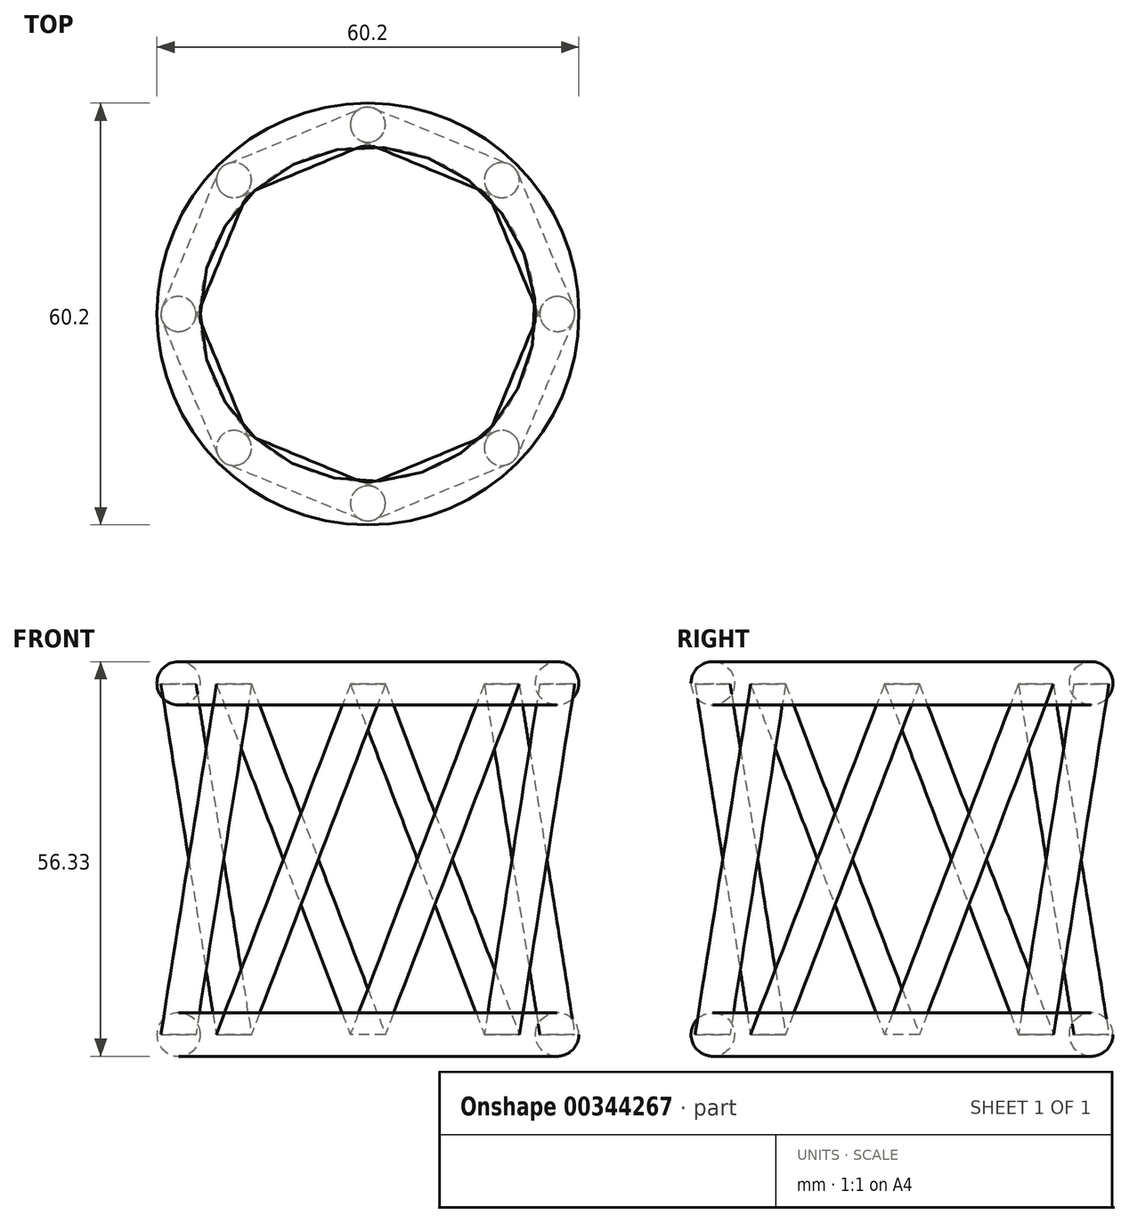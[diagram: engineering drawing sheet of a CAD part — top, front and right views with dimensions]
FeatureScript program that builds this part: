
annotation { "Feature Type Name" : "Feature", "Feature Type Description" : "" }
export const myFeature = defineFeature(function(context is Context, id is Id, definition is map)
    precondition{}
    {
        {
            var Q0;
            Q0=qCreatedBy(makeId("Top.planeOp"),FACE);
            var sketch = newSketch(context, id + "F0", { "sketchPlane" : qUnion([Q0])});
            skCircle(sketch, "E0", {"center": v(0, -27.04) * mm, "radius": 2.5 * mm});
            skCircle(sketch, "E1.1.0", {"center": v(10.35, -24.98) * mm, "radius": 2.5 * mm});
            skCircle(sketch, "E1.2.0", {"center": v(19.12, -19.12) * mm, "radius": 2.5 * mm});
            skCircle(sketch, "E1.3.0", {"center": v(24.98, -10.35) * mm, "radius": 2.5 * mm});
            skCircle(sketch, "E1.4.0", {"center": v(27.04, 0) * mm, "radius": 2.5 * mm});
            skCircle(sketch, "E1.5.0", {"center": v(24.98, 10.35) * mm, "radius": 2.5 * mm});
            skCircle(sketch, "E1.6.0", {"center": v(19.12, 19.12) * mm, "radius": 2.5 * mm});
            skCircle(sketch, "E1.7.0", {"center": v(10.35, 24.98) * mm, "radius": 2.5 * mm});
            skCircle(sketch, "E1.8.0", {"center": v(0, 27.04) * mm, "radius": 2.5 * mm});
            skCircle(sketch, "E1.9.0", {"center": v(-10.35, 24.98) * mm, "radius": 2.5 * mm});
            skCircle(sketch, "E1.10.0", {"center": v(-19.12, 19.12) * mm, "radius": 2.5 * mm});
            skCircle(sketch, "E1.11.0", {"center": v(-24.98, 10.35) * mm, "radius": 2.5 * mm});
            skCircle(sketch, "E1.12.0", {"center": v(-27.04, 0) * mm, "radius": 2.5 * mm});
            skCircle(sketch, "E1.13.0", {"center": v(-24.98, -10.35) * mm, "radius": 2.5 * mm});
            skCircle(sketch, "E1.14.0", {"center": v(-19.12, -19.12) * mm, "radius": 2.5 * mm});
            skCircle(sketch, "E1.15.0", {"center": v(-10.35, -24.98) * mm, "radius": 2.5 * mm});
            skPoint(sketch, "E1.center", {"position": v(0, 0) * mm});
            skLineSegment(sketch, "E2", {"start": v(0, -27.04) * mm, "end": v(0, 27.04) * mm});
            skSolve(sketch);
        }
        {
            var Q0;
            Q0=qCreatedBy(makeId("Top.planeOp"),FACE);
            cPlane(context, id + "F1", {"entities" : qUnion([Q0]), "cplaneType" : CPlaneType.OFFSET, "offset" : 50 * mm, "width" : 150 * mm, "height" : 150 * mm});
        }
        {
            var Q0;
            Q0=qCreatedBy(id+"F1.planeOp",FACE);
            var sketch = newSketch(context, id + "F2", { "sketchPlane" : qUnion([Q0])});
            skCircle(sketch, "E3", {"center": v(0, -27.02) * mm, "radius": 2.5 * mm});
            skCircle(sketch, "E4.1.0", {"center": v(10.34, -24.96) * mm, "radius": 2.5 * mm});
            skCircle(sketch, "E4.2.0", {"center": v(19.1, -19.1) * mm, "radius": 2.5 * mm});
            skCircle(sketch, "E4.3.0", {"center": v(24.96, -10.34) * mm, "radius": 2.5 * mm});
            skCircle(sketch, "E4.4.0", {"center": v(27.02, 0) * mm, "radius": 2.5 * mm});
            skCircle(sketch, "E4.5.0", {"center": v(24.96, 10.34) * mm, "radius": 2.5 * mm});
            skCircle(sketch, "E4.6.0", {"center": v(19.1, 19.1) * mm, "radius": 2.5 * mm});
            skCircle(sketch, "E4.7.0", {"center": v(10.34, 24.96) * mm, "radius": 2.5 * mm});
            skCircle(sketch, "E4.8.0", {"center": v(0, 27.02) * mm, "radius": 2.5 * mm});
            skCircle(sketch, "E4.9.0", {"center": v(-10.34, 24.96) * mm, "radius": 2.5 * mm});
            skCircle(sketch, "E4.10.0", {"center": v(-19.1, 19.1) * mm, "radius": 2.5 * mm});
            skCircle(sketch, "E4.11.0", {"center": v(-24.96, 10.34) * mm, "radius": 2.5 * mm});
            skCircle(sketch, "E4.12.0", {"center": v(-27.02, 0) * mm, "radius": 2.5 * mm});
            skCircle(sketch, "E4.13.0", {"center": v(-24.96, -10.34) * mm, "radius": 2.5 * mm});
            skCircle(sketch, "E4.14.0", {"center": v(-19.1, -19.1) * mm, "radius": 2.5 * mm});
            skCircle(sketch, "E4.15.0", {"center": v(-10.34, -24.96) * mm, "radius": 2.5 * mm});
            skPoint(sketch, "E4.center", {"position": v(0, 0) * mm});
            skLineSegment(sketch, "E5", {"start": v(19.1, -19.1) * mm, "end": v(-19.1, 19.1) * mm});
            skSolve(sketch);
        }
        {
            var Q0;
            Q0=sQuery(id+"F0.wireOp",VERTEX,"E0.center");
            var Q1;
            Q1=sQuery(id+"F2.wireOp",VERTEX,"E4.2.0.center");
            var Q2;
            Q2=sQuery(id+"F2.wireOp",VERTEX,"E5.end");
            cPlane(context, id + "F3", {"entities" : qUnion([Q0, Q1, Q2]), "cplaneType" : CPlaneType.THREE_POINT, "offset" : 25 * mm, "width" : 150 * mm, "height" : 150 * mm});
        }
        {
            var Q0;
            Q0=qCreatedBy(id+"F3.planeOp",FACE);
            var sketch = newSketch(context, id + "F4", { "sketchPlane" : qUnion([Q0])});
            skLineSegment(sketch, "E6", {"start": v(-15.7, -12.86) * mm, "end": v(-41.15, 34.9) * mm});
            skSolve(sketch);
        }
        {
            var Q0;
            Q0=qCreatedBy(makeId("Front.planeOp"),FACE);
            var sketch = newSketch(context, id + "F5", { "sketchPlane" : qUnion([Q0])});
            skLineSegment(sketch, "E7", {"start": v(0, 0) * mm, "end": v(0, 50.82) * mm});
            skSolve(sketch);
        }
        {
            var Q0;
            Q0=makeQuery(id+"F0.imprint","IMPRINT",FACE,{"disambiguationData":[TD([[makeQuery(id+"F0.imprint","IMPRINT",EDGE,{"derivedFrom":sQuery(id+"F0.wireOp",EDGE,"E0")}),1.0]])]});
            var Q1;
            Q1=makeQuery(id+"F2.imprint","IMPRINT",FACE,{"disambiguationData":[TD([[makeQuery(id+"F2.imprint","IMPRINT",EDGE,{"derivedFrom":sQuery(id+"F2.wireOp",EDGE,"E4.2.0")}),1.0]])]});
            var Q2;
            Q2=sQuery(id+"F4.wireOp",EDGE,"E6");
            sweep(context, id + "F6", {"profiles" : qUnion([Q0, Q1]), "path" : qUnion([Q2]), "keepProfileOrientation" : true});
        }
        {
            var Q0;
            Q0=makeQuery(id+"F6.opSweep","SWEPT_BODY",BODY,{"disambiguationData":[OSD([sQuery(id+"F2.wireOp",EDGE,"E4.2.0"),sQuery(id+"F4.wireOp",EDGE,"E6")])]});
            deleteBodies(context, id + "F7", {"entities" : qUnion([Q0])});
        }
        {
            var Q0;
            Q0=makeQuery(id+"F6.opSweep","SWEPT_BODY",BODY,{"disambiguationData":[OSD([sQuery(id+"F0.wireOp",EDGE,"E0"),sQuery(id+"F4.wireOp",EDGE,"E6")])]});
            var Q1;
            Q1=sQuery(id+"F5.wireOp",EDGE,"E7");
            circularPattern(context, id + "F8", {"entities" : qUnion([Q0]), "axis" : qUnion([Q1]), "angle" : 360 * degree, "instanceCount" : 8, "equalSpace" : true});
        }
        {
            var Q0;
            Q0=qCreatedBy(makeId("Front.planeOp"),FACE);
            var sketch = newSketch(context, id + "F9", { "sketchPlane" : qUnion([Q0])});
            skCircle(sketch, "E8", {"center": v(-27, 50.13) * mm, "radius": 3.1 * mm});
            skCircle(sketch, "E9", {"center": v(-27, 0) * mm, "radius": 3.1 * mm});
            skSolve(sketch);
        }
        {
            var Q0;
            Q0=makeQuery(id+"F9.imprint","IMPRINT",FACE,{"disambiguationData":[TD([[makeQuery(id+"F9.imprint","IMPRINT",EDGE,{"derivedFrom":sQuery(id+"F9.wireOp",EDGE,"E8")}),1.0]])]});
            var Q1;
            Q1=makeQuery(id+"F9.imprint","IMPRINT",FACE,{"disambiguationData":[TD([[makeQuery(id+"F9.imprint","IMPRINT",EDGE,{"derivedFrom":sQuery(id+"F9.wireOp",EDGE,"E9")}),1.0]])]});
            var Q2;
            Q2=sQuery(id+"F5.wireOp",EDGE,"E7");
            revolve(context, id + "F10", {"entities" : qUnion([Q0, Q1]), "axis" : qUnion([Q2]), "revolveType" : RevolveType.FULL});
        }
    });
